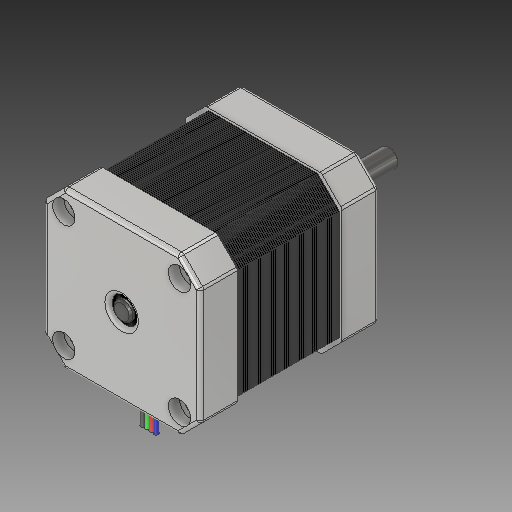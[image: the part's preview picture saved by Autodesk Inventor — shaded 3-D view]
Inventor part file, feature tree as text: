
AUTODESK INVENTOR PART (.ipt)
format: ipt  version: 2018 (Build 220112000, 112)  size: 1,367,552 bytes
history: native  units: mm
features: sketch x5, other x3
ambient origin geometry x8: Origin, YZ Plane, XZ Plane, XY Plane, X Axis, Y Axis, Z Axis, Center Point
bodies: Solid1 (feature_tree)
feature tree (8):
  other  "M1173041- NEMA 17.ipt"
  other  "Solid1::M1173041- NEMA 17.ipt"
  other  "TaggingFeature1"
  sketch  "Sketch1"  dims[d0=10.0mm]
  sketch  "Sketch4"
  sketch  "Sketch5"
  sketch  "Sketch6"
  sketch  "Sketch11"
